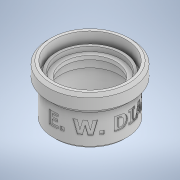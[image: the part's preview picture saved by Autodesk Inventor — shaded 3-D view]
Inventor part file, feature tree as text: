
AUTODESK INVENTOR PART (.ipt)
format: ipt  version: 2021 (Build 250183000, 183)  size: 340,480 bytes
history: native  units: mm
features: sketch x7, extrude x6, chamfer x3, emboss x1
ambient origin geometry x8: Origin, YZ Plane, XZ Plane, XY Plane, X Axis, Y Axis, Z Axis, Center Point
bodies: Solid1 (feature_tree)
feature tree (17):
  extrude  "Extrusion1"  Depth=3.0mm
  extrude  "Extrusion2"  Depth=39.0mm
  chamfer  "Chamfer1"  Distance=7.5mm
  extrude  "Extrusion3"  Depth=28.0mm
  extrude  "Extrusion4"  Depth=31.4mm
  extrude  "Extrusion5"  Depth=1.5mm
  chamfer  "Chamfer2"  Distance=5.0mm
  extrude  "Extrusion6"  Depth=1.5mm TaperAngle=45.0deg
  chamfer  "Chamfer3"  Distance=5.0mm
  emboss  "Emboss1"
  sketch  "Sketch1"  dims[d0=33.6mm d1=3.0mm]
  sketch  "Sketch2"  dims[d2=20.0mm d3=0.0mm d4=39.0mm]
  sketch  "Sketch3"  dims[d5=3.0mm d6=7.5mm d7=0.0mm]
  sketch  "Sketch4"  dims[d8=2.7mm d9=2.0mm d10=45.0deg d11=28.0mm]
  sketch  "Sketch5"  dims[d12=2.0mm d13=0.0mm d14=31.4mm]
  sketch  "Sketch6"  dims[d15=5.0mm d16=0.0mm d17=1.5mm]
  sketch  "Sketch7"  dims[d18=3.0mm d19=5.0mm d20=0.0mm d21=1.5mm d22=2.0mm d23=45.0deg d24=5.0mm d25=0.0mm d26=1.5mm d27=2.0mm d28=45.0deg d29=0.5mm d30=0.0mm]
